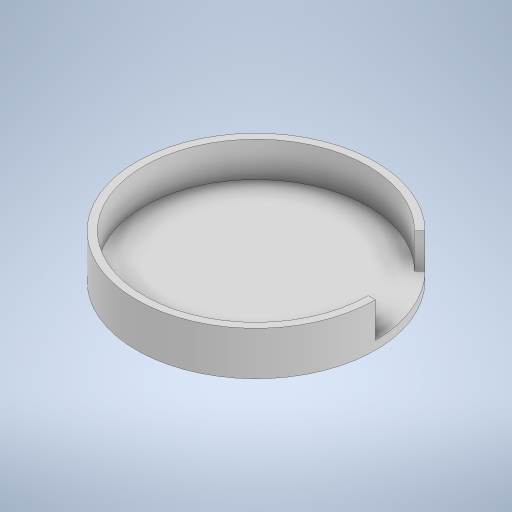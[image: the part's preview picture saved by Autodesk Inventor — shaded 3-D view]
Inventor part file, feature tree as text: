
AUTODESK INVENTOR PART (.ipt)
format: ipt  version: 2024 (Build 280153000, 153)  size: 251,392 bytes
history: native  units: in
note: dims shown in document units (in); Inventor stores cm internally (conversion verified against a paired STEP export)
features: extrude x3, sketch x3
ambient origin geometry x8: Origin, YZ Plane, XZ Plane, XY Plane, X Axis, Y Axis, Z Axis, Center Point
bodies: Body1 (feature_tree)
feature tree (6):
  extrude  "Extrusion3"  Depth=3.2283in
  extrude  "Extrusion4"  Depth=0.1181in
  extrude  "Extrusion5"  Depth=0.5906in TaperAngle=0.0deg
  sketch  "Sketch1"  dims[d0=3.0315in d1=3.2283in]
  sketch  "Sketch3"  dims[d7=0.1181in d8=0.0in d9=3.2283in]
  sketch  "Sketch4"  dims[d10=3.0315in d11=0.5906in d12=0.0in d13=1.6142in d14=45.0deg d15=0.5906in d16=0.0in]
